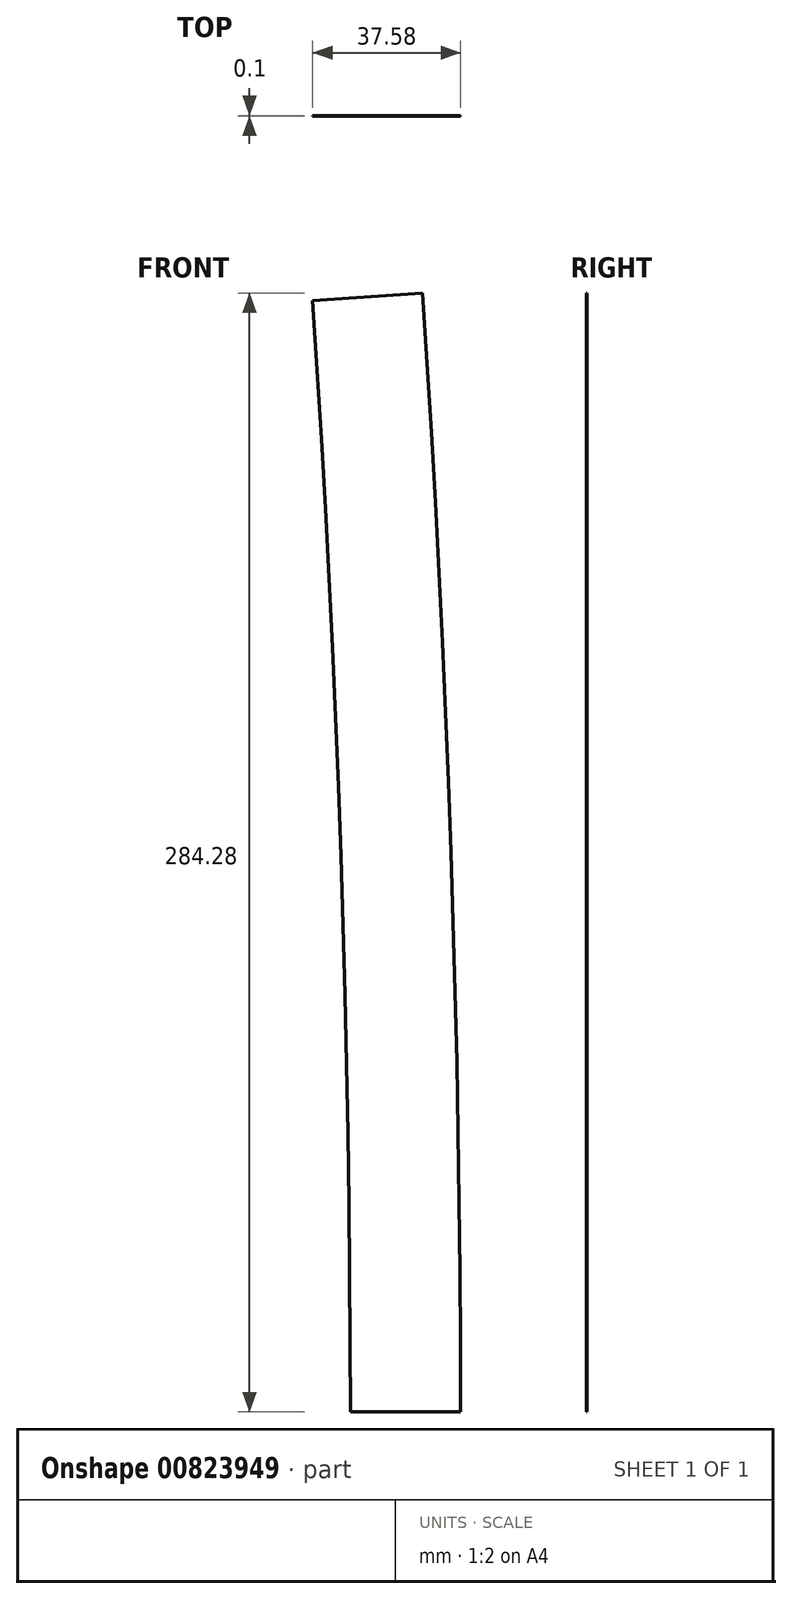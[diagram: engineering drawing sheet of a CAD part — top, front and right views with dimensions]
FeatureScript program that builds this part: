
annotation { "Feature Type Name" : "Feature", "Feature Type Description" : "" }
export const myFeature = defineFeature(function(context is Context, id is Id, definition is map)
    precondition{}
    {
        {
            var Q0;
            Q0=qCreatedBy(makeId("Front.planeOp"),FACE);
            var sketch = newSketch(context, id + "F0", { "sketchPlane" : qUnion([Q0])});
            skLineSegment(sketch, "E0", {"start": v(-28, 0) * mm, "end": v(0, 0) * mm});
            skLineSegment(sketch, "E1", {"start": v(-37.58, 282.38) * mm, "end": v(-9.65, 284.28) * mm});
            skArc(sketch, "E2", {"start": v(0, 0) * mm, "mid": v(-2.41, 142.22) * mm, "end": v(-9.65, 284.28) * mm});
            skArc(sketch, "E3", {"start": v(-28, 0) * mm, "mid": v(-30.4, 141.27) * mm, "end": v(-37.58, 282.38) * mm});
            skLineSegment(sketch, "E4", {"start": v(-4192.63, 0) * mm, "end": v(-9.65, 284.28) * mm, "construction": true});
            skSolve(sketch);
        }
        {
            var Q0;
            Q0=makeQuery(id+"F0.imprint","IMPRINT",FACE,{"disambiguationData":[TD([[makeQuery(id+"F0.imprint","IMPRINT",EDGE,{"derivedFrom":sQuery(id+"F0.wireOp",EDGE,"E0")}),1.0]])]});
            extrude(context, id + "F1", {"entities" : qUnion([Q0]), "depth" : 0.1 * mm, "offsetDistance" : 25 * mm});
        }
    });
